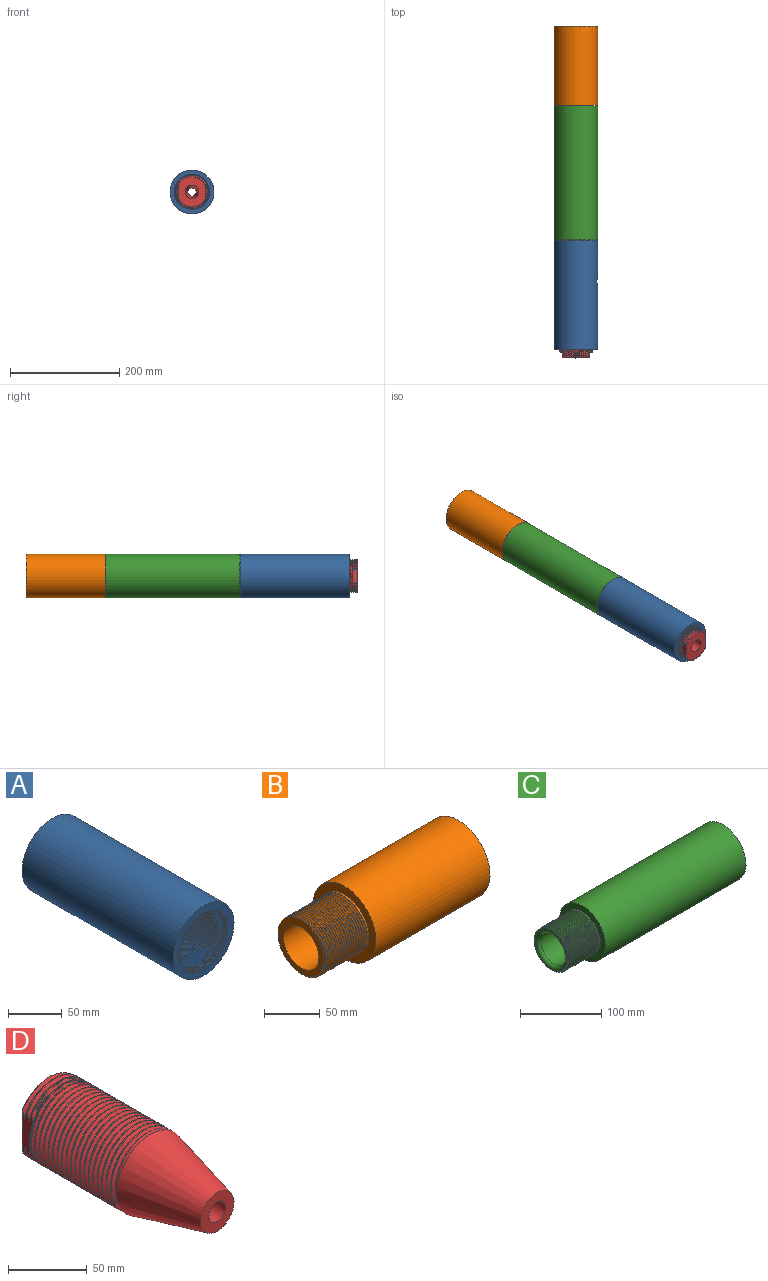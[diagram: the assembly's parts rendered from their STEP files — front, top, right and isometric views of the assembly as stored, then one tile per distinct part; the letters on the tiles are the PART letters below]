
ASSEMBLY  parts=4 mates=2
PART A: 64 faces, bbox 83.2x205.3x82 mm
  f0: cylinder r=31mm len=62mm, axis (0,-1,0), area 468.7mm2, adj f1,f60,f61,f62,f63
  f1: cylinder r=31mm len=62mm, axis (0,-1,0), area 198.3mm2, adj f0,f2,f60,f62
  f2: cylinder r=31mm len=62mm, axis (0,-1,0), area 198.3mm2, adj f1,f3,f60,f62
  f3: cylinder r=31mm len=62mm, axis (0,-1,0), area 198.3mm2, adj f2,f4,f60,f62
  f4: cylinder r=31mm len=62mm, axis (0,-1,0), area 198.3mm2, adj f3,f5,f60,f62
  f5: cylinder r=31mm len=62mm, axis (0,-1,0), area 198.2mm2, adj f4,f6,f60,f62
  f6: cylinder r=31mm len=62mm, axis (0,-1,0), area 198.2mm2, adj f5,f7,f60,f62
  f7: cylinder r=31mm len=62mm, axis (0,-1,0), area 198.3mm2, adj f6,f8,f60,f62
  f8: cylinder r=31mm len=62mm, axis (0,-1,0), area 198.3mm2, adj f7,f9,f60,f62
  f9: cylinder r=31mm len=62mm, axis (0,-1,0), area 198.2mm2, adj f8,f10,f60,f62
  f10: cylinder r=31mm len=62mm, axis (0,-1,0), area 198.2mm2, adj f9,f11,f60,f62
  f11: cylinder r=31mm len=62mm, axis (0,-1,0), area 198.3mm2, adj f10,f12,f60,f62
  f12: cylinder r=31mm len=62mm, axis (0,-1,0), area 198.3mm2, adj f11,f13,f60,f62
  f13: cylinder r=31mm len=62mm, axis (0,-1,0), area 198.3mm2, adj f12,f14,f60,f62
  f14: cylinder r=31mm len=62mm, axis (0,-1,0), area 198.3mm2, adj f13,f15,f60,f62
  f15: cylinder r=31mm len=62mm, axis (0,-1,0), area 198.3mm2, adj f14,f16,f60,f62
  f16: cylinder r=31mm len=62mm, axis (0,-1,0), area 198.3mm2, adj f15,f17,f60,f62
  f17: cylinder r=31mm len=62mm, axis (0,-1,0), area 198.3mm2, adj f16,f18,f60,f62
  f18: cylinder r=31mm len=62mm, axis (0,-1,0), area 198.3mm2, adj f17,f19,f60,f62
  f19: cylinder r=31mm len=62mm, axis (0,-1,0), area 66.8mm2, adj f18,f20,f60,f62
  f20: plane 82.05x82.05mm, normal (0,-1,0), area 1823.8mm2, adj f19,f21,f59,f60,f62
  f21: cylinder r=40mm len=200mm, axis (0,1,0), area 49852.8mm2, adj f20,f22,f23,f24,f53,f54,f55,f56
  f22: bspline ~20.35x6.33mm, area 0mm2, adj f21,f23
  f23: bspline ~24.5x18.19mm, area 15.2mm2, adj f21,f22,f24
  f24: bspline ~27.14x23.5mm, area 311.3mm2, adj f21,f23,f25,f52,f53,f54
  f25: bspline ~25.02x21.67mm, area 98.4mm2, adj f24,f26,f51,f52
  f26: cylinder r=30mm len=69mm, axis (0,1,0), area 12059.1mm2, adj f25,f27,f48,f49,f50,f51,f52,f63
  f27: bspline ~83.3x74.48mm, area 10334.3mm2, adj f26,f28,f30,f31,f32,f33,f34,f35
  f28: cylinder r=30mm len=60mm, axis (0,1,0), area 100.9mm2, adj f27,f29,f30,f49
  f29: cylinder r=30mm len=24.76mm, axis (0,1,0), area 6.8mm2, adj f28,f49,f58
  f30: cylinder r=30mm len=60mm, axis (0,1,0), area 101mm2, adj f27,f28,f31,f49
  f31: cylinder r=30mm len=60mm, axis (0,1,0), area 101.1mm2, adj f27,f30,f32,f49
  f32: cylinder r=30mm len=60mm, axis (0,1,0), area 101mm2, adj f27,f31,f33,f49
  f33: cylinder r=30mm len=60mm, axis (0,1,0), area 101mm2, adj f27,f32,f34,f49
  f34: cylinder r=30mm len=60mm, axis (0,1,0), area 101.1mm2, adj f27,f33,f35,f49
  f35: cylinder r=30mm len=60mm, axis (0,1,0), area 101mm2, adj f27,f34,f36,f49
  f36: cylinder r=30mm len=60mm, axis (0,1,0), area 100.9mm2, adj f27,f35,f37,f49
  f37: cylinder r=30mm len=60mm, axis (0,1,0), area 101mm2, adj f27,f36,f38,f49
  f38: cylinder r=30mm len=60mm, axis (0,1,0), area 101mm2, adj f27,f37,f39,f49
  f39: cylinder r=30mm len=60mm, axis (0,1,0), area 101mm2, adj f27,f38,f40,f49
  f40: cylinder r=30mm len=60mm, axis (0,1,0), area 101.1mm2, adj f27,f39,f41,f49
  f41: cylinder r=30mm len=60mm, axis (0,1,0), area 101.1mm2, adj f27,f40,f42,f49
  f42: cylinder r=30mm len=60mm, axis (0,1,0), area 101mm2, adj f27,f41,f43,f49
  f43: cylinder r=30mm len=60mm, axis (0,1,0), area 101mm2, adj f27,f42,f44,f49
  f44: cylinder r=30mm len=60mm, axis (0,1,0), area 101mm2, adj f27,f43,f45,f49
  f45: cylinder r=30mm len=60mm, axis (0,1,0), area 100.9mm2, adj f27,f44,f46,f49
  f46: cylinder r=30mm len=60mm, axis (0,1,0), area 100.9mm2, adj f27,f45,f48,f49
  f47: bspline ~81.53x75.34mm, area 4282.7mm2, adj f27,f49,f50,f58
  f48: cylinder r=30mm len=60mm, axis (0,1,0), area 101mm2, adj f26,f27,f46,f49
  f49: bspline ~81.3x74.48mm, area 10027.5mm2, adj f26,f28,f29,f30,f31,f32,f33,f34
  f50: plane 3.5x2.54mm, normal (0,0,1), area 5mm2, adj f26,f27,f47,f49
  f51: cylinder r=9.5mm len=19mm, axis (-1,0,0), area 102.7mm2, adj f25,f26,f52
  f52: plane 2.73x2.54mm, normal (0,0,-1), area 4mm2, adj f24,f25,f26,f51,f53,f54
  f53: bspline ~27.14x23.5mm, area 240mm2, adj f21,f24,f52,f54
  f54: bspline ~28x24.25mm, area 287.1mm2, adj f21,f24,f52,f53,f55
  f55: bspline ~23.74x17.63mm, area 20mm2, adj f21,f54,f57
  f56: bspline ~21x6.25mm, area 0mm2, adj f21,f57
  f57: bspline ~20.35x6.33mm, area 10.7mm2, adj f21,f55,f56
  f58: plane 81.27x81.27mm, normal (0,1,0), area 1954.8mm2, adj f21,f27,f29,f47,f49
  f59: bspline ~77.37x67mm, area 2181.8mm2, adj f20,f60,f61,f62
  f60: bspline ~76.79x66.5mm, area 10233.8mm2, adj f0,f1,f2,f3,f4,f5,f6,f7
  f61: plane 2.5x1.74mm, normal (0,0,1), area 2.5mm2, adj f0,f59,f60,f62
  f62: bspline ~77.37x67mm, area 10113.3mm2, adj f0,f1,f2,f3,f4,f5,f6,f7
  f63: plane 62x62mm, normal (0,-1,0), area 191.6mm2, adj f0,f26
PART B: 14 faces, bbox 202.3x81.3x81.3 mm
  f0: cylinder r=31mm len=62mm, axis (-1,0,0), area 543.3mm2, adj f2,f7,f10,f11,f12
  f1: bspline ~60.71x60.68mm, area 6690.1mm2, adj f2,f3,f8,f9,f10,f12
  f2: bspline ~71.59x62mm, area 133.8mm2, adj f0,f1,f10,f12
  f3: plane 59.92x59.7mm, normal (-1,0,0), area 1099.1mm2, adj f1,f8,f9,f13
  f4: cylinder r=40mm len=145mm, axis (-1,0,0), area 36442.5mm2, adj f6,f7
  f5: cone r=15mm half-angle=4.3deg, axis (1,0,0), area 16539.7mm2, adj f6,f13
  f6: plane 80x80mm, normal (1,0,0), area 2199.1mm2, adj f4,f5
  f7: plane 80x80mm, normal (-1,0,0), area 2007.5mm2, adj f0,f4
  f8: bspline ~70.16x60.76mm, area 6493.3mm2, adj f1,f3,f9,f12
  f9: bspline ~66.4x57.5mm, area 3545.9mm2, adj f1,f3,f8,f11
  f10: plane 12.24x2.89mm, normal (-0.87,-0.5,0), area 20.2mm2, adj f0,f1,f2,f11
  f11: cylinder r=0.5mm len=12.2mm, axis (0,0,1), area 12.6mm2, adj f0,f9,f10,f12
  f12: plane 11.94x1.97mm, normal (0.87,-0.5,0), area 15.5mm2, adj f0,f1,f2,f8,f11
  f13: cylinder r=22.5mm len=100mm, axis (-1,0,0), area 14137.2mm2, adj f3,f5
PART C: 21 faces, bbox 303.7x81.3x81.3 mm
  f0: cylinder r=31mm len=62mm, axis (1,0,0), area 462.6mm2, adj f14,f18,f19
  f1: cylinder r=22.5mm len=240mm, axis (-1,0,0), area 33929.2mm2, adj f14,f20
  f2: cylinder r=31mm len=62mm, axis (-1,0,0), area 543.3mm2, adj f4,f8,f11,f12,f13
  f3: bspline ~60.71x60.68mm, area 6690.1mm2, adj f4,f5,f9,f10,f11,f13
  f4: bspline ~71.59x62mm, area 133.8mm2, adj f2,f3,f11,f13
  f5: plane 59.92x59.7mm, normal (-1,0,0), area 313.7mm2, adj f3,f9,f10,f20
  f6: cylinder r=40mm len=245mm, axis (-1,0,0), area 61575.2mm2, adj f7,f8
  f7: plane 81.08x81.08mm, normal (1,0,0), area 1656.3mm2, adj f6,f15,f16,f17
  f8: plane 80x80mm, normal (-1,0,0), area 2007.5mm2, adj f2,f6
  f9: bspline ~70.16x60.76mm, area 6493.3mm2, adj f3,f5,f10,f13
  f10: bspline ~66.4x57.5mm, area 3545.9mm2, adj f3,f5,f9,f12
  f11: plane 12.24x2.89mm, normal (-0.87,-0.5,0), area 20.2mm2, adj f2,f3,f4,f12
  f12: cylinder r=0.5mm len=12.2mm, axis (0,0,1), area 12.6mm2, adj f2,f10,f11,f13
  f13: plane 11.94x1.97mm, normal (0.87,-0.5,0), area 15.5mm2, adj f2,f3,f4,f9,f12
  f14: plane 62x62mm, normal (1,0,0), area 1428.6mm2, adj f0,f1
  f15: bspline ~76.79x66.5mm, area 7439.2mm2, adj f7,f16,f17,f18,f19
  f16: bspline ~77.65x67.25mm, area 4193.1mm2, adj f7,f15,f17,f18
  f17: bspline ~76.79x66.5mm, area 7168.9mm2, adj f7,f15,f16,f18
  f18: plane 3.15x2.54mm, normal (0,0,1), area 4.8mm2, adj f0,f15,f16,f17,f19
  f19: bspline ~73.02x63.24mm, area 140.5mm2, adj f0,f15,f18
  f20: torus R=27.5mm, axis (-1,0,0), area 1200mm2, adj f1,f5
PART D: 55 faces, bbox 60.6x152.3x69.9 mm
  f0: cylinder r=30mm len=50mm, axis (0,1,0), area 31.7mm2, adj f8,f19,f52,f53
  f1: cylinder r=30mm len=50mm, axis (0,1,0), area 31.7mm2, adj f7,f18,f52,f53
  f2: cylinder r=30mm len=50mm, axis (0,1,0), area 31.7mm2, adj f10,f21,f52,f53
  f3: cylinder r=30mm len=50mm, axis (0,1,0), area 31.7mm2, adj f9,f20,f52,f53
  f4: cylinder r=30mm len=25mm, axis (0,1,0), area 9.1mm2, adj f5,f11,f47,f52
  f5: plane 58.16x50.59mm, normal (0,1,0), area 1962.1mm2, adj f4,f6,f11,f12,f18,f43,f47,f52
  f6: bspline ~25.98x16.13mm, area 0mm2, adj f5,f12,f53
  f7: bspline ~60x34.64mm, area 158mm2, adj f1,f13,f52,f53
  f8: bspline ~60x34.64mm, area 158mm2, adj f0,f14,f52,f53
  f9: bspline ~60x34.64mm, area 158mm2, adj f3,f16,f52,f53
  f10: bspline ~79.97x69.28mm, area 9106.8mm2, adj f2,f17,f24,f25,f26,f27,f28,f29
  f11: bspline ~60x34.64mm, area 138.2mm2, adj f4,f5,f15,f52,f53
  f12: bspline ~41.63x32.04mm, area 20.5mm2, adj f5,f6,f18,f53
  f13: bspline ~55.5x32.04mm, area 65.5mm2, adj f7,f19,f52,f53
  f14: bspline ~55.5x32.04mm, area 65.5mm2, adj f8,f22,f52,f53
  f15: bspline ~55.5x32.04mm, area 65.5mm2, adj f11,f20,f52,f53
  f16: bspline ~55.5x32.04mm, area 65.5mm2, adj f9,f21,f52,f53
  f17: bspline ~79.53x64.09mm, area 3532.6mm2, adj f10,f22,f49,f53
  f18: bspline ~60x34.64mm, area 145.1mm2, adj f1,f5,f12,f52,f53
  f19: bspline ~60x34.64mm, area 158mm2, adj f0,f13,f52,f53
  f20: bspline ~60x34.64mm, area 158mm2, adj f3,f15,f52,f53
  f21: bspline ~60x34.64mm, area 158mm2, adj f2,f16,f52,f53
  f22: bspline ~81.97x69.28mm, area 9341.9mm2, adj f14,f17,f23,f24,f25,f26,f27,f28
  f23: cylinder r=30mm len=60mm, axis (0,1,0), area 635.6mm2, adj f22,f24,f46,f48,f49,f50
  f24: cylinder r=30mm len=60mm, axis (0,1,0), area 101.1mm2, adj f10,f22,f23,f25
  f25: cylinder r=30mm len=60mm, axis (0,1,0), area 100.9mm2, adj f10,f22,f24,f26
  f26: cylinder r=30mm len=60mm, axis (0,1,0), area 101.4mm2, adj f10,f22,f25,f27
  f27: cylinder r=30mm len=60mm, axis (0,1,0), area 100.9mm2, adj f10,f22,f26,f28
  f28: cylinder r=30mm len=60mm, axis (0,1,0), area 100.7mm2, adj f10,f22,f27,f29
  f29: cylinder r=30mm len=60mm, axis (0,1,0), area 101.2mm2, adj f10,f22,f28,f30
  f30: cylinder r=30mm len=60mm, axis (0,1,0), area 101mm2, adj f10,f22,f29,f31
  f31: cylinder r=30mm len=60mm, axis (0,1,0), area 101.2mm2, adj f10,f22,f30,f32
  f32: cylinder r=30mm len=60mm, axis (0,1,0), area 100.9mm2, adj f10,f22,f31,f33
  f33: cylinder r=30mm len=60mm, axis (0,1,0), area 100.6mm2, adj f10,f22,f32,f34
  f34: cylinder r=30mm len=60mm, axis (0,1,0), area 101.3mm2, adj f10,f22,f33,f35
  f35: cylinder r=30mm len=60mm, axis (0,1,0), area 101.1mm2, adj f10,f22,f34,f36
  f36: cylinder r=30mm len=60mm, axis (0,1,0), area 101mm2, adj f10,f22,f35,f37
  f37: cylinder r=30mm len=60mm, axis (0,1,0), area 101mm2, adj f10,f22,f36,f38
  f38: cylinder r=30mm len=60mm, axis (0,1,0), area 100.7mm2, adj f10,f22,f37,f39
  f39: cylinder r=30mm len=60mm, axis (0,1,0), area 101.3mm2, adj f10,f22,f38,f40
  f40: cylinder r=30mm len=60mm, axis (0,1,0), area 101.2mm2, adj f10,f22,f39,f41
  f41: cylinder r=30mm len=60mm, axis (0,1,0), area 100.8mm2, adj f10,f22,f40,f42
  f42: cylinder r=30mm len=60mm, axis (0,1,0), area 91.6mm2, adj f10,f22,f41,f52
  f43: cylinder r=12.5mm len=90mm, axis (0,1,0), area 7068.6mm2, adj f5,f45
  f44: plane 30x30mm, normal (0,-1,0), area 530.1mm2, adj f45,f46
  f45: cone r=12.5mm half-angle=4.8deg, axis (0,1,0), area 3783mm2, adj f43,f44
  f46: cone r=15mm half-angle=14deg, axis (0,1,0), area 8743.4mm2, adj f23,f44
  f47: bspline ~25.98x16.13mm, area 0.4mm2, adj f4,f5,f52
  f48: plane 11.4x2.25mm, normal (-0.5,0.87,0), area 19.9mm2, adj f22,f23,f49
  f49: cylinder r=0.5mm len=11.99mm, axis (0,0,1), area 12.3mm2, adj f17,f23,f48,f50
  f50: plane 11.4x2.25mm, normal (-0.5,-0.87,0), area 19.9mm2, adj f10,f23,f49
  f51: plane 27.02x3.82mm, normal (0,1,0), area 58.8mm2, adj f10,f52
  f52: plane 33.39x10.23mm, normal (-1,0,0), area 287.1mm2, adj f0,f1,f2,f3,f4,f5,f7,f8
  f53: plane 33.39x10.23mm, normal (1,0,0), area 276.7mm2, adj f0,f1,f2,f3,f5,f6,f7,f8
  f54: plane 30.85x4.82mm, normal (0,1,0), area 86.3mm2, adj f22,f53
PLACE A rot(axis=(1,0,0),180deg) t=(98.6,-8.05,-585.68)mm
PLACE B rot(axis=(0.58,0.58,0.58),120deg) t=(98.6,383.37,-585.68)mm
PLACE C rot(axis=(0.58,0.58,0.58),120deg) t=(98.6,137.3,-585.68)mm
PLACE D rot(axis=(-1,0,0),180deg) t=(98.6,-23.67,-585.68)mm
MATE cylindrical D.f46 <-> A.f26  axis (0,1,0) through (98.6,126.33,-585.68)mm
MATE slider C.f1 <-> B.f13  axis (0,1,0) through (98.6,437.3,-585.68)mm
